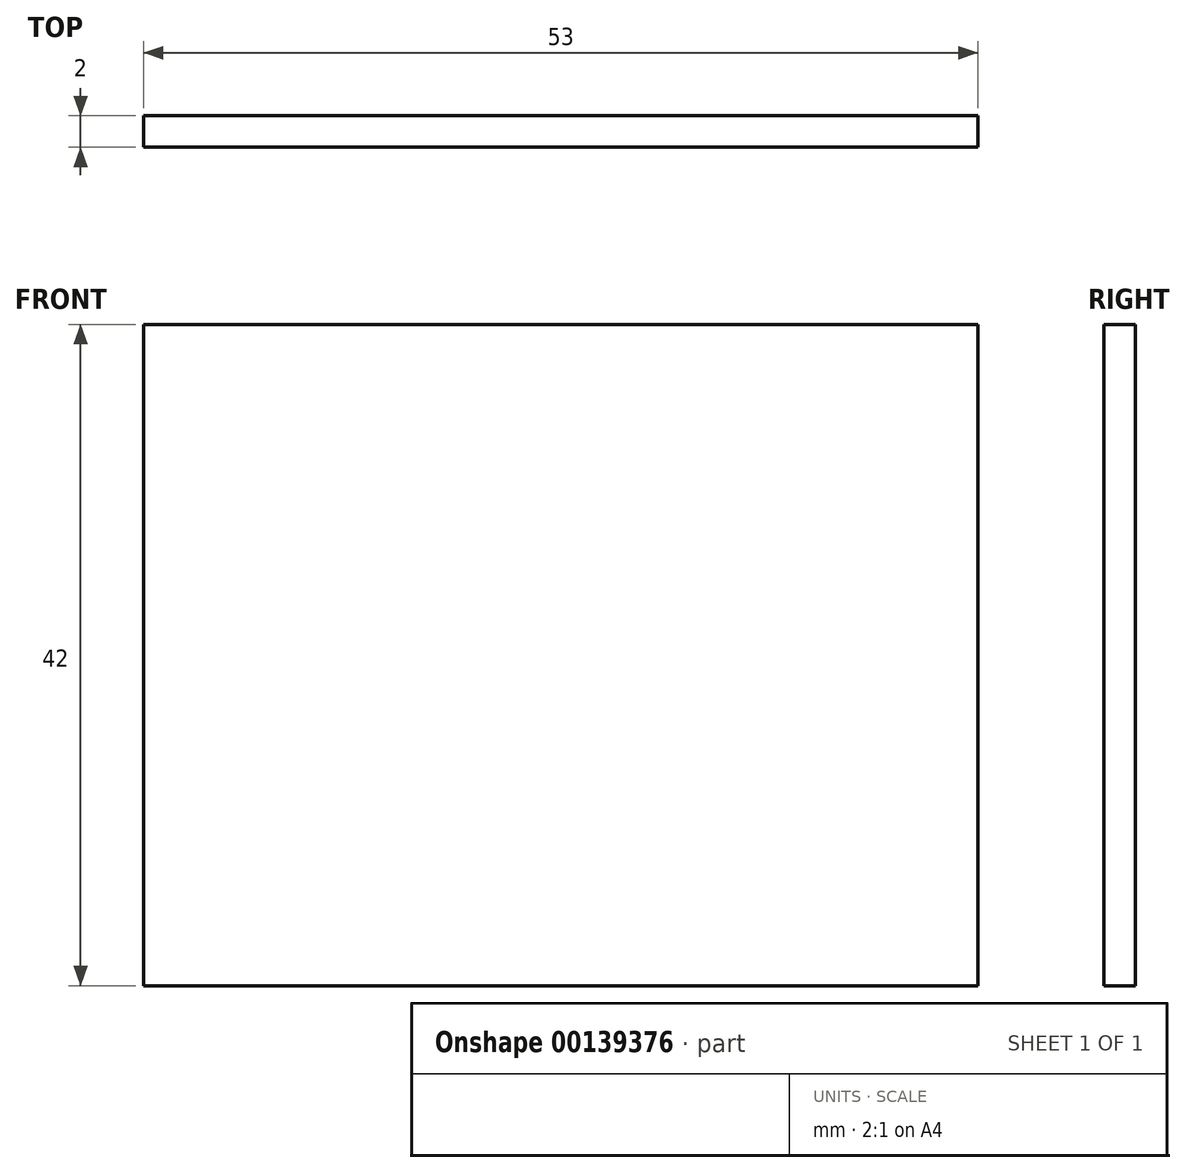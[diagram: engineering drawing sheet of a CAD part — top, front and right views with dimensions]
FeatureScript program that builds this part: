
annotation { "Feature Type Name" : "Feature", "Feature Type Description" : "" }
export const myFeature = defineFeature(function(context is Context, id is Id, definition is map)
    precondition{}
    {
        {
            var Q0;
            Q0=qCreatedBy(makeId("Front.planeOp"),FACE);
            var sketch = newSketch(context, id + "F0", { "sketchPlane" : qUnion([Q0])});
            skLineSegment(sketch, "E0.bottom", {"start": v(-53, 42) * mm, "end": v(0, 42) * mm});
            skLineSegment(sketch, "E0.top", {"start": v(-53, 0) * mm, "end": v(0, 0) * mm});
            skLineSegment(sketch, "E0.left", {"start": v(-53, 42) * mm, "end": v(-53, 0) * mm});
            skLineSegment(sketch, "E0.right", {"start": v(0, 42) * mm, "end": v(0, 0) * mm});
            skSolve(sketch);
        }
        {
            var Q0;
            Q0=makeQuery(id+"F0.imprint","IMPRINT",FACE,{"disambiguationData":[TD([[makeQuery(id+"F0.imprint","IMPRINT",EDGE,{"derivedFrom":sQuery(id+"F0.wireOp",EDGE,"E0.bottom")}),-1.0]])]});
            extrude(context, id + "F1", {"entities" : qUnion([Q0]), "depth" : 2 * mm});
        }
    });
